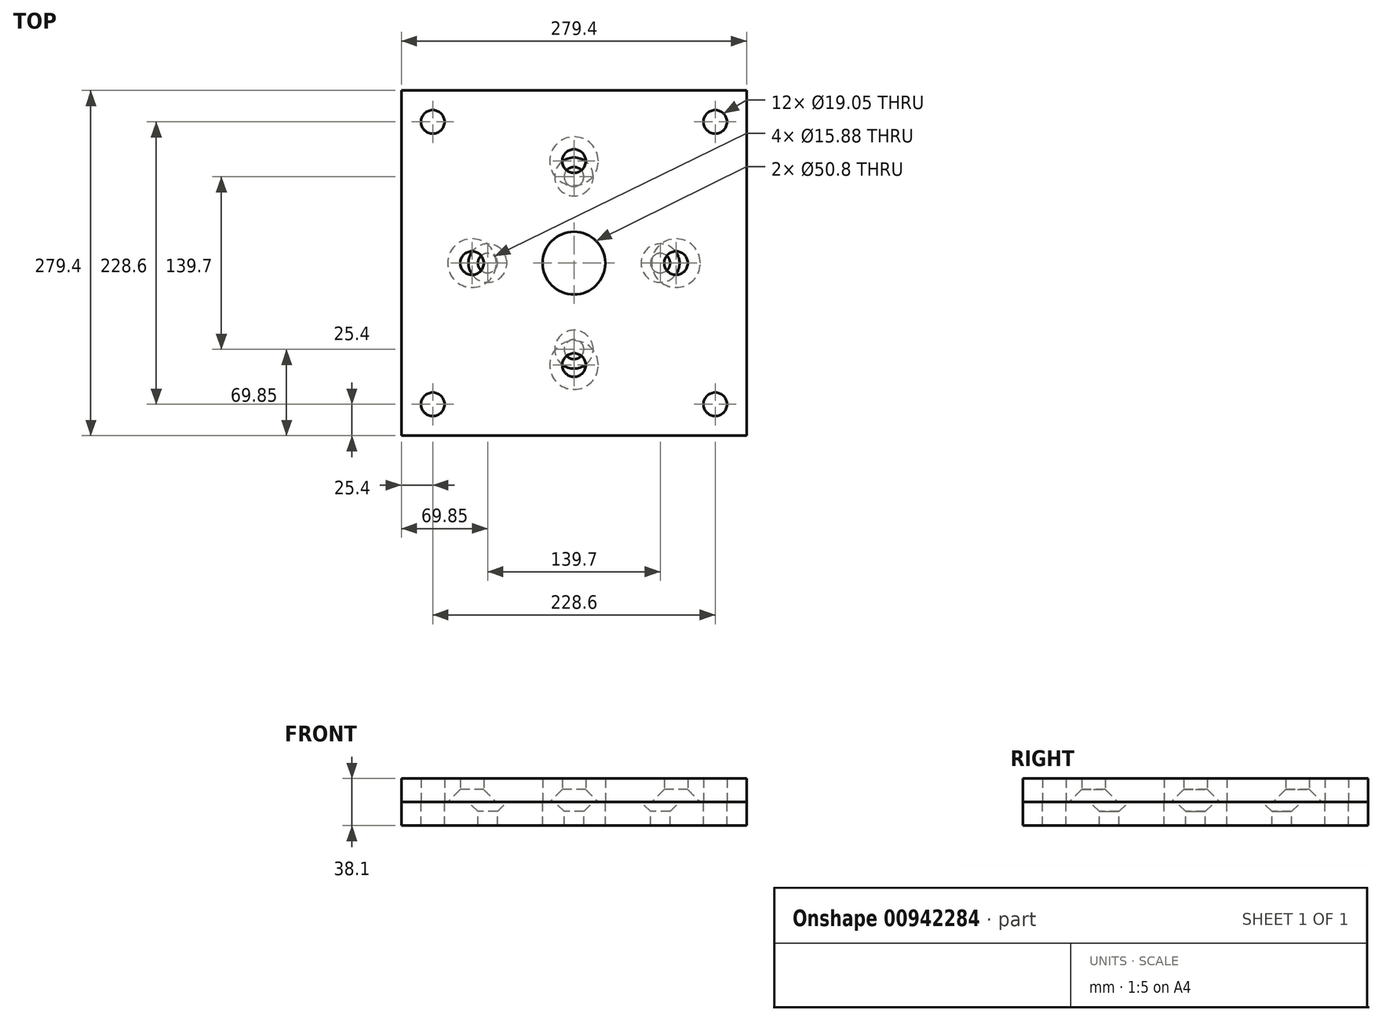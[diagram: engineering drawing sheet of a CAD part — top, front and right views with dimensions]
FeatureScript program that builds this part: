
annotation { "Feature Type Name" : "Feature", "Feature Type Description" : "" }
export const myFeature = defineFeature(function(context is Context, id is Id, definition is map)
    precondition{}
    {
        {
            var Q0;
            Q0=qCreatedBy(makeId("Top.planeOp"),FACE);
            var sketch = newSketch(context, id + "F0", { "sketchPlane" : qUnion([Q0])});
            skLineSegment(sketch, "E0.bottom", {"start": v(139.7, -139.7) * mm, "end": v(-139.7, -139.7) * mm});
            skLineSegment(sketch, "E0.top", {"start": v(139.7, 139.7) * mm, "end": v(-139.7, 139.7) * mm});
            skLineSegment(sketch, "E0.left", {"start": v(139.7, -139.7) * mm, "end": v(139.7, 139.7) * mm});
            skLineSegment(sketch, "E0.right", {"start": v(-139.7, -139.7) * mm, "end": v(-139.7, 139.7) * mm});
            skPoint(sketch, "E0.middle", {"position": v(0, 0) * mm});
            skCircle(sketch, "E1", {"center": v(0, 0) * mm, "radius": 82.55 * mm});
            skCircle(sketch, "E2", {"center": v(0, 0) * mm, "radius": 118.11 * mm});
            skCircle(sketch, "E3", {"center": v(0, 82.55) * mm, "radius": 9.53 * mm});
            skCircle(sketch, "E4", {"center": v(0, -82.55) * mm, "radius": 9.53 * mm});
            skCircle(sketch, "E5", {"center": v(82.55, 0) * mm, "radius": 9.53 * mm});
            skCircle(sketch, "E6", {"center": v(-82.55, 0) * mm, "radius": 9.53 * mm});
            skCircle(sketch, "E7", {"center": v(-114.3, 114.3) * mm, "radius": 9.53 * mm});
            skCircle(sketch, "E8", {"center": v(114.3, 114.3) * mm, "radius": 9.53 * mm});
            skCircle(sketch, "E9", {"center": v(-114.3, -114.3) * mm, "radius": 9.53 * mm});
            skCircle(sketch, "E10", {"center": v(114.3, -114.3) * mm, "radius": 9.53 * mm});
            skCircle(sketch, "E11", {"center": v(0, 0) * mm, "radius": 25.4 * mm});
            skSolve(sketch);
        }
        {
            var Q0;
            Q0 = qSketchRegion(id + "F0", true);
            var Q1;
            Q1=makeQuery(id+"F0.imprint","IMPRINT",FACE,{"disambiguationData":[TD([[makeQuery(id+"F0.imprint","IMPRINT",EDGE,{"derivedFrom":sQuery(id+"F0.wireOp",EDGE,"E2")}),1.0]])]});
            var Q2;
            Q2=makeQuery(id+"F0.imprint","IMPRINT",FACE,{"disambiguationData":[TD([[makeQuery(id+"F0.imprint","IMPRINT",EDGE,{"derivedFrom":sQuery(id+"F0.wireOp",EDGE,"E11")}),-1.0]])]});
            extrude(context, id + "F1", {"entities" : qUnion([Q0, Q1, Q2]), "depth" : 19.05 * mm, "offsetDistance" : 25.4 * mm});
        }
        {
            var Q0;
            Q0=makeQuery(id+"F1.opExtrude","CAP_EDGE",EDGE,{"disambiguationData":[OSD([sQuery(id+"F0.wireOp",EDGE,"E4")])],"isStart":true});
            var Q1;
            Q1=makeQuery(id+"F1.opExtrude","CAP_EDGE",EDGE,{"disambiguationData":[OSD([sQuery(id+"F0.wireOp",EDGE,"E5")])],"isStart":true});
            var Q2;
            Q2=makeQuery(id+"F1.opExtrude","CAP_EDGE",EDGE,{"disambiguationData":[OSD([sQuery(id+"F0.wireOp",EDGE,"E3")])],"isStart":true});
            var Q3;
            Q3=makeQuery(id+"F1.opExtrude","CAP_EDGE",EDGE,{"disambiguationData":[OSD([sQuery(id+"F0.wireOp",EDGE,"E6")])],"isStart":true});
            chamfer(context, id + "F2", {"entities" : qUnion([Q0, Q1, Q2, Q3]), "width" : 10.16 * mm, "tangentPropagation" : true});
        }
        {
            var Q0;
            Q0=qCreatedBy(makeId("Top.planeOp"),FACE);
            var sketch = newSketch(context, id + "F3", { "sketchPlane" : qUnion([Q0])});
            skLineSegment(sketch, "E12.bottom", {"start": v(139.7, -139.7) * mm, "end": v(-139.7, -139.7) * mm});
            skLineSegment(sketch, "E12.top", {"start": v(139.7, 139.7) * mm, "end": v(-139.7, 139.7) * mm});
            skLineSegment(sketch, "E12.left", {"start": v(139.7, -139.7) * mm, "end": v(139.7, 139.7) * mm});
            skLineSegment(sketch, "E12.right", {"start": v(-139.7, -139.7) * mm, "end": v(-139.7, 139.7) * mm});
            skPoint(sketch, "E12.middle", {"position": v(0, 0) * mm});
            skCircle(sketch, "E13", {"center": v(0, 0) * mm, "radius": 69.85 * mm});
            skCircle(sketch, "E14", {"center": v(69.85, 0) * mm, "radius": 7.94 * mm});
            skCircle(sketch, "E15", {"center": v(-69.85, 0) * mm, "radius": 7.94 * mm});
            skCircle(sketch, "E16", {"center": v(0, 69.85) * mm, "radius": 7.94 * mm});
            skCircle(sketch, "E17", {"center": v(0, -69.85) * mm, "radius": 7.94 * mm});
            skCircle(sketch, "E18", {"center": v(-114.3, 114.3) * mm, "radius": 9.53 * mm});
            skCircle(sketch, "E19", {"center": v(114.3, 114.3) * mm, "radius": 9.53 * mm});
            skCircle(sketch, "E20", {"center": v(114.3, -114.3) * mm, "radius": 9.53 * mm});
            skCircle(sketch, "E21", {"center": v(-114.3, -114.3) * mm, "radius": 9.53 * mm});
            skCircle(sketch, "E22", {"center": v(0, 0) * mm, "radius": 25.4 * mm});
            skSolve(sketch);
        }
        {
            var Q0;
            Q0 = qSketchRegion(id + "F3", true);
            var Q1;
            Q1=makeQuery(id+"F3.imprint","IMPRINT",FACE,{"disambiguationData":[TD([[makeQuery(id+"F3.imprint","IMPRINT",EDGE,{"derivedFrom":sQuery(id+"F3.wireOp",EDGE,"E22")}),-1.0]])]});
            extrude(context, id + "F4", {"entities" : qUnion([Q0, Q1]), "oppositeDirection" : true, "depth" : 19.05 * mm, "offsetDistance" : 25.4 * mm});
        }
        {
            var Q0;
            Q0=makeQuery(id+"F4.opExtrude","CAP_EDGE",EDGE,{"disambiguationData":[OSD([sQuery(id+"F3.wireOp",EDGE,"E15")])],"isStart":true});
            var Q1;
            Q1=makeQuery(id+"F4.opExtrude","CAP_EDGE",EDGE,{"disambiguationData":[OSD([sQuery(id+"F3.wireOp",EDGE,"E16")])],"isStart":true});
            var Q2;
            Q2=makeQuery(id+"F4.opExtrude","CAP_EDGE",EDGE,{"disambiguationData":[OSD([sQuery(id+"F3.wireOp",EDGE,"E14")])],"isStart":true});
            var Q3;
            Q3=makeQuery(id+"F4.opExtrude","CAP_EDGE",EDGE,{"disambiguationData":[OSD([sQuery(id+"F3.wireOp",EDGE,"E17")])],"isStart":true});
            chamfer(context, id + "F5", {"entities" : qUnion([Q0, Q1, Q2, Q3]), "width" : 7.62 * mm, "tangentPropagation" : true});
        }
    });
